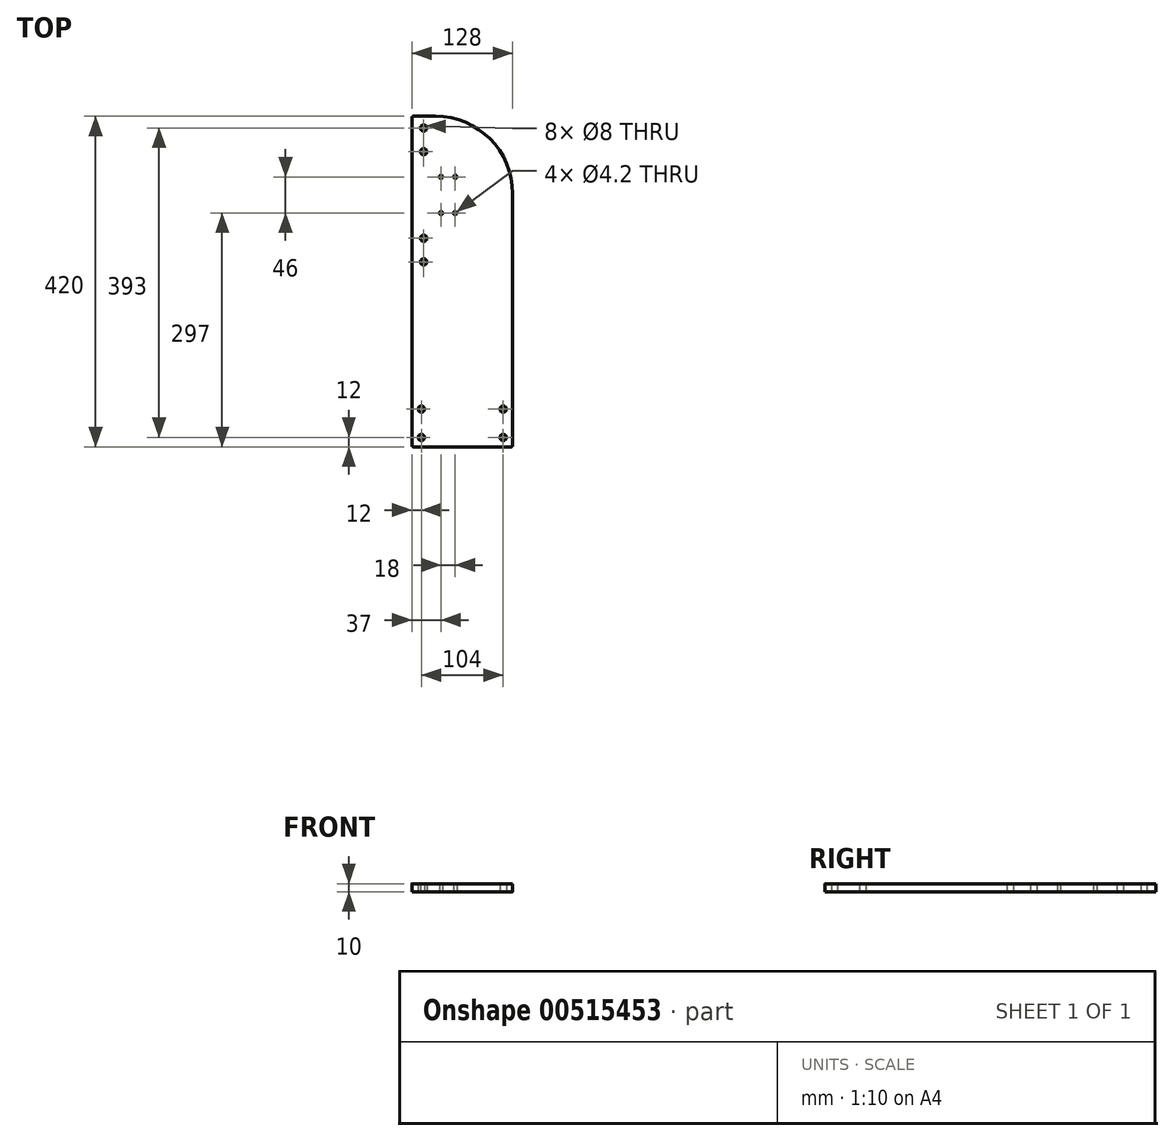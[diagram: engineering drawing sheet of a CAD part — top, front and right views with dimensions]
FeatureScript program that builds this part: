
annotation { "Feature Type Name" : "Feature", "Feature Type Description" : "" }
export const myFeature = defineFeature(function(context is Context, id is Id, definition is map)
    precondition{}
    {
        {
            var Q0;
            Q0=qCreatedBy(makeId("Top.planeOp"),FACE);
            var sketch = newSketch(context, id + "F0", { "sketchPlane" : qUnion([Q0])});
            skLineSegment(sketch, "E0.bottom", {"start": v(2, 0) * mm, "end": v(126, 0) * mm});
            skLineSegment(sketch, "E0.top", {"start": v(2, 420) * mm, "end": v(30, 420) * mm});
            skLineSegment(sketch, "E0.left", {"start": v(0, 2) * mm, "end": v(0, 418) * mm});
            skLineSegment(sketch, "E0.right", {"start": v(128, 2) * mm, "end": v(128, 322) * mm});
            skCircle(sketch, "E1", {"center": v(15, 405) * mm, "radius": 4 * mm});
            skCircle(sketch, "E2", {"center": v(15, 375) * mm, "radius": 4 * mm});
            skLineSegment(sketch, "E3", {"start": v(128, 320) * mm, "end": v(0, 320) * mm, "construction": true});
            skCircle(sketch, "E4.MirrorC", {"center": v(15, 235) * mm, "radius": 4 * mm});
            skCircle(sketch, "E5.MirrorC", {"center": v(15, 265) * mm, "radius": 4 * mm});
            skLineSegment(sketch, "E6", {"start": v(64, 0) * mm, "end": v(64, 420) * mm, "construction": true});
            skCircle(sketch, "E7", {"center": v(12, 12) * mm, "radius": 4 * mm});
            skCircle(sketch, "E8", {"center": v(12, 48) * mm, "radius": 4 * mm});
            skCircle(sketch, "E9.MirrorC", {"center": v(116, 48) * mm, "radius": 4 * mm});
            skCircle(sketch, "E10.MirrorC", {"center": v(116, 12) * mm, "radius": 4 * mm});
            skPoint(sketch, "E11.visualSharp", {"position": v(128, 420) * mm});
            skArc(sketch, "E11.filletArc", {"start": v(128, 322) * mm, "mid": v(99.3, 391.3) * mm, "end": v(30, 420) * mm});
            skLineSegment(sketch, "E12", {"start": v(55, 0) * mm, "end": v(55, 420) * mm, "construction": true});
            skPoint(sketch, "E13.newPointA", {"position": v(0, 0) * mm});
            skLineSegment(sketch, "E14", {"start": v(0, 418) * mm, "end": v(0, 2) * mm});
            skPoint(sketch, "E15.visualSharp", {"position": v(0, 420) * mm});
            skArc(sketch, "E15.filletArc", {"start": v(2, 420) * mm, "mid": v(0.59, 419.41) * mm, "end": v(0, 418) * mm});
            skPoint(sketch, "E16.visualSharp", {"position": v(128, 0) * mm});
            skArc(sketch, "E16.filletArc", {"start": v(126, 0) * mm, "mid": v(127.41, 0.59) * mm, "end": v(128, 2) * mm});
            skLineSegment(sketch, "E17", {"start": v(0, 125) * mm, "end": v(128, 125) * mm, "construction": true});
            skArc(sketch, "E18.filletArc", {"start": v(0, 2) * mm, "mid": v(0.59, 0.59) * mm, "end": v(2, 0) * mm});
            skCircle(sketch, "E19", {"center": v(55, 343) * mm, "radius": 2.1 * mm});
            skCircle(sketch, "E20.MirrorC", {"center": v(55, 297) * mm, "radius": 2.1 * mm});
            skCircle(sketch, "E21", {"center": v(37, 343) * mm, "radius": 2.1 * mm});
            skCircle(sketch, "E22.MirrorC", {"center": v(37, 297) * mm, "radius": 2.1 * mm});
            skSolve(sketch);
        }
        {
            var Q0;
            Q0=qSketchRegion(id+"F0",true);
            extrude(context, id + "F1", {"entities" : qUnion([Q0]), "depth" : 10 * mm});
        }
    });
